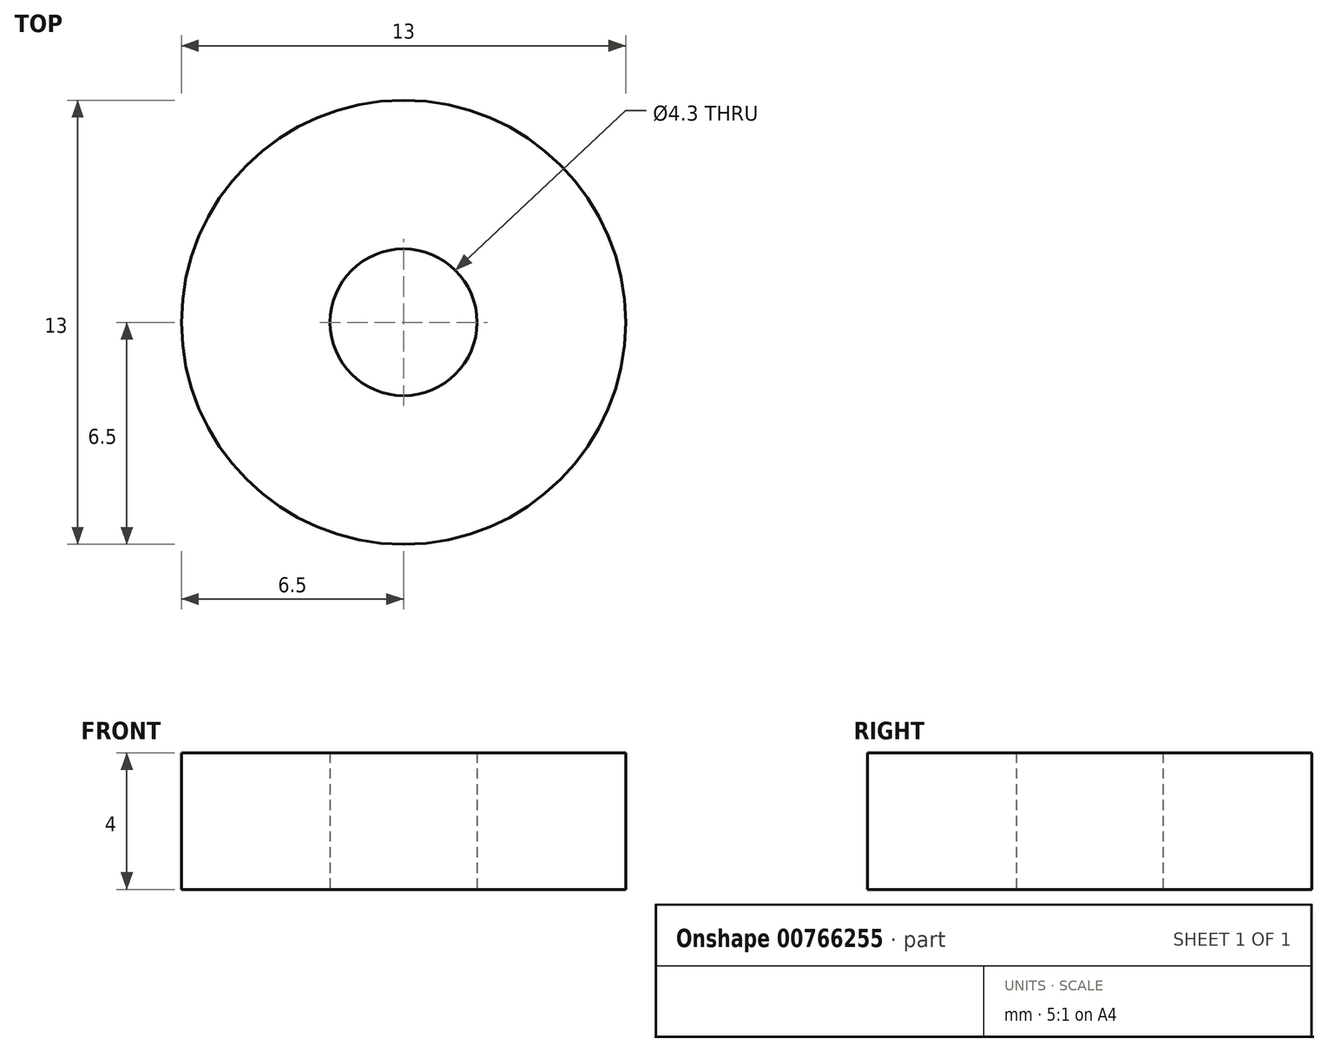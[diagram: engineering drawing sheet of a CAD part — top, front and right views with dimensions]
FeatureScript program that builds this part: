
annotation { "Feature Type Name" : "Feature", "Feature Type Description" : "" }
export const myFeature = defineFeature(function(context is Context, id is Id, definition is map)
    precondition{}
    {
        {
            var Q0;
            Q0=qCreatedBy(makeId("Top.planeOp"),FACE);
            var sketch = newSketch(context, id + "F0", { "sketchPlane" : qUnion([Q0])});
            skCircle(sketch, "E0", {"center": v(0, 0) * mm, "radius": 2.15 * mm});
            skCircle(sketch, "E1", {"center": v(0, 0) * mm, "radius": 6.5 * mm});
            skSolve(sketch);
        }
        {
            var Q0;
            Q0=qSketchRegion(id+"F0",true);
            extrude(context, id + "F1", {"entities" : qUnion([Q0]), "depth" : 4 * mm, "offsetDistance" : 25 * mm});
        }
    });
